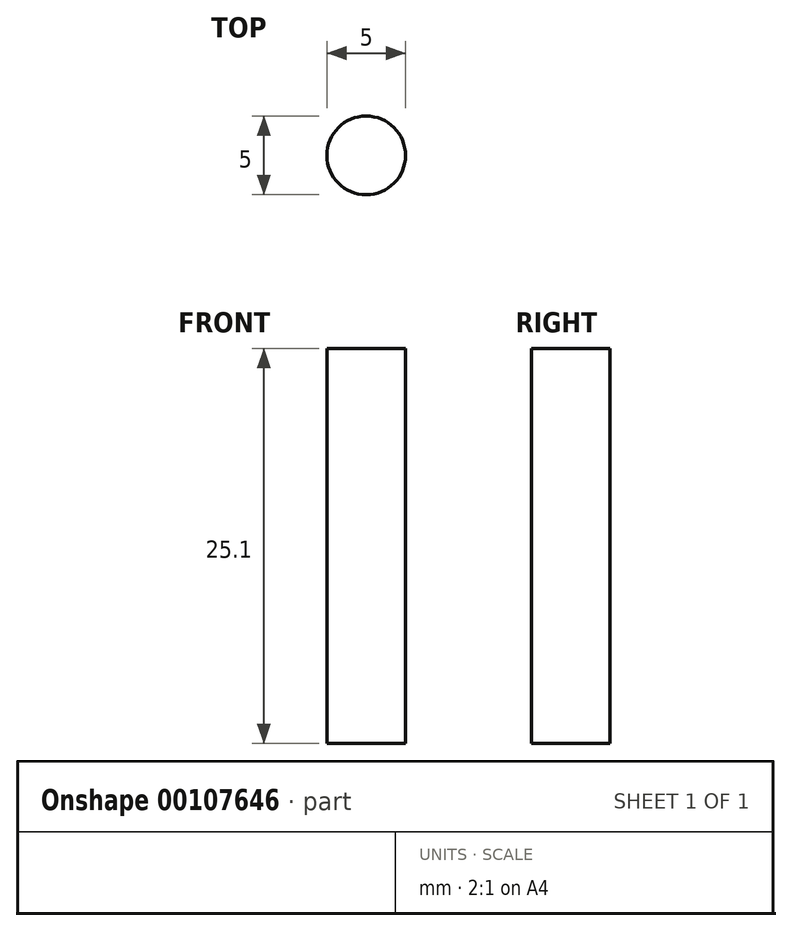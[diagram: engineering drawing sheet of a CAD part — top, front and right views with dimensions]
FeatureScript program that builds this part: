
annotation { "Feature Type Name" : "Feature", "Feature Type Description" : "" }
export const myFeature = defineFeature(function(context is Context, id is Id, definition is map)
    precondition{}
    {
        {
            var Q0;
            Q0=qCreatedBy(makeId("Top.planeOp"),FACE);
            var sketch = newSketch(context, id + "F0", { "sketchPlane" : qUnion([Q0])});
            skCircle(sketch, "E0", {"center": v(0, 0) * mm, "radius": 2.5 * mm});
            skSolve(sketch);
        }
        {
            var Q0;
            Q0=makeQuery(id+"F0.imprint","IMPRINT",FACE,{"disambiguationData":[TD([[makeQuery(id+"F0.imprint","IMPRINT",EDGE,{"derivedFrom":sQuery(id+"F0.wireOp",EDGE,"E0")}),1.0]])]});
            extrude(context, id + "F1", {"entities" : qUnion([Q0]), "depth" : 25.1 * mm});
        }
    });
